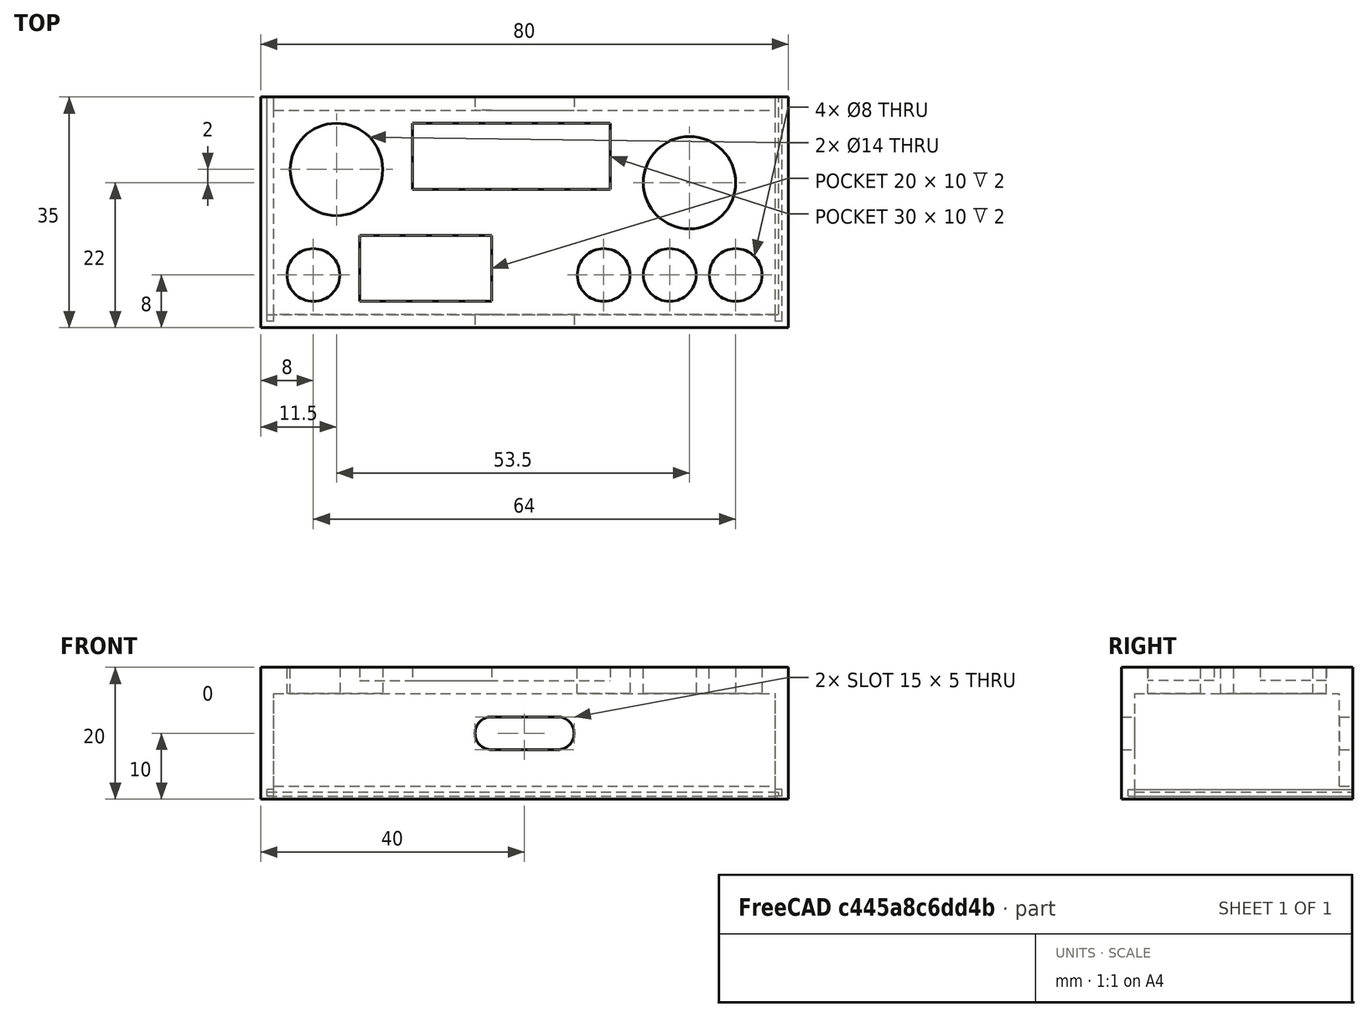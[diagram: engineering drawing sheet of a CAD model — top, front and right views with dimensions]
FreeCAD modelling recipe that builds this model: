
FCSTD DOCUMENT  (FreeCAD 1.0R39109 (Git))
Label: CriticalArtefactVersion3
License: All rights reserved
LicenseURL: https://en.wikipedia.org/wiki/All_rights_reserved
objects: Sketcher::SketchObject×5, Part::Box×5, Part::Cut×4, PartDesign::Pocket×3, Mesh::Feature×2, PartDesign::Pad×1, PartDesign::Body×1
note: 32 computed .brp shape members not serialized (recipe doc carries the construction recipe); baked Part::Feature solids carry a one-line shape summary decoded from their .brp

FEATURE [Sketcher::SketchObject] Sketch
  ArcFitTolerance = 1e-06
  AttachmentSupport = -> [XY_Plane]
  FullyConstrained = true
  MakeInternals = false
  MapMode = 5
  sketch-geometry (4):
    g0: LineSegment StartX=0 StartY=35 StartZ=0 EndX=0 EndY=0 EndZ=0
    g1: LineSegment StartX=0 StartY=0 StartZ=0 EndX=80 EndY=0 EndZ=0
    g2: LineSegment StartX=80 StartY=0 StartZ=0 EndX=80 EndY=35 EndZ=0
    g3: LineSegment StartX=80 StartY=35 StartZ=0 EndX=0 EndY=35 EndZ=0
  constraints (11):
    c: Coincident(g0,g1)
    c: Coincident(g1,g2)
    c: Coincident(g2,g3)
    c: Coincident(g3,g0)
    c: Vertical(g0)
    c: Vertical(g2)
    c: Horizontal(g1)
    c: Horizontal(g3)
    c: DistanceY(g0,g0) = 35
    c: DistanceX(g3,g3) = 80
    c: Coincident(g0,g-1)
FEATURE [PartDesign::Pad] Pad
  Direction = (0,0,1)
  Length = 20
  Length2 = 10
  Profile = -> Sketch
  ReferenceAxis = -> Sketch [N_Axis]
  Refine = true
  Suppressed = false
  Type = 0
FEATURE [Sketcher::SketchObject] Sketch001
  ArcFitTolerance = 1e-06
  AttachmentSupport = -> [Pad]
  ExternalGeometry = -> [Pad]
  FullyConstrained = true
  MakeInternals = false
  MapMode = 5
  Placement = pos=(0,0,20) rot=(0,0,1;0rad)
  sketch-geometry (6):
    g0: Circle CenterX=11.5 CenterY=24 CenterZ=0 NormalX=0 NormalY=0 NormalZ=1 AngleXU=0 Radius=7
    g1: Circle CenterX=8 CenterY=8 CenterZ=0 NormalX=0 NormalY=0 NormalZ=1 AngleXU=0 Radius=4
    g2: Circle CenterX=65 CenterY=22 CenterZ=0 NormalX=0 NormalY=0 NormalZ=1 AngleXU=0 Radius=7
    g3: Circle CenterX=52 CenterY=8 CenterZ=0 NormalX=0 NormalY=0 NormalZ=1 AngleXU=0 Radius=4
    g4: Circle CenterX=62 CenterY=8 CenterZ=0 NormalX=0 NormalY=0 NormalZ=1 AngleXU=0 Radius=4
    g5: Circle CenterX=72 CenterY=8 CenterZ=0 NormalX=0 NormalY=0 NormalZ=1 AngleXU=0 Radius=4
  constraints (18):
    c: Diameter(g0) = 14
    c: Distance(g0,g-4) = 11.5
    c: Distance(g0,g-3) = 11
    c: Diameter(g1) = 8
    c: Distance(g1,g-4) = 8
    c: Distance(g1,g-5) = 8
    c: Diameter(g2) = 14
    c: Distance(g2,g-6) = 15
    c: Distance(g2,g-3) = 13
    c: Diameter(g5) = 8
    c: Diameter(g4) = 8
    c: Diameter(g3) = 8
    c: Distance(g5,g-5) = 8
    c: Distance(g4,g-5) = 8
    c: Distance(g3,g-5) = 8
    c: Distance(g5,g-6) = 8
    c: Distance(g5,g4) = 10
    c: Distance(g3,g4) = 10
FEATURE [PartDesign::Pocket] Pocket
  BaseFeature = -> Pad
  Direction = (0,0,-1)
  Length = 33
  Length2 = 5
  Profile = -> Sketch001
  ReferenceAxis = -> Sketch001 [N_Axis]
  Refine = true
  Suppressed = false
  Type = 0
FEATURE [Sketcher::SketchObject] Sketch002
  ArcFitTolerance = 1e-06
  AttachmentSupport = -> [Pocket]
  ExternalGeometry = -> [Pocket,Sketch001]
  FullyConstrained = true
  MakeInternals = false
  MapMode = 5
  Placement = pos=(0,0,20) rot=(0,0,1;0rad)
  sketch-geometry (8):
    g0: LineSegment StartX=23 StartY=31 StartZ=0 EndX=23 EndY=21 EndZ=0
    g1: LineSegment StartX=23 StartY=21 StartZ=0 EndX=53 EndY=21 EndZ=0
    g2: LineSegment StartX=53 StartY=21 StartZ=0 EndX=53 EndY=31 EndZ=0
    g3: LineSegment StartX=53 StartY=31 StartZ=0 EndX=23 EndY=31 EndZ=0
    g4: LineSegment StartX=15 StartY=14 StartZ=0 EndX=15 EndY=4 EndZ=0
    g5: LineSegment StartX=15 StartY=4 StartZ=0 EndX=35 EndY=4 EndZ=0
    g6: LineSegment StartX=35 StartY=4 StartZ=0 EndX=35 EndY=14 EndZ=0
    g7: LineSegment StartX=35 StartY=14 StartZ=0 EndX=15 EndY=14 EndZ=0
  constraints (24):
    c: Coincident(g0,g1)
    c: Coincident(g1,g2)
    c: Coincident(g2,g3)
    c: Coincident(g3,g0)
    c: Vertical(g0)
    c: Vertical(g2)
    c: Horizontal(g1)
    c: Horizontal(g3)
    c: Coincident(g4,g5)
    c: Coincident(g5,g6)
    c: Coincident(g6,g7)
    c: Coincident(g7,g4)
    c: Vertical(g4)
    c: Vertical(g6)
    c: Horizontal(g5)
    c: Horizontal(g7)
    c: DistanceX(g3,g3) = 30
    c: DistanceX(g7,g7) = 20
    c: DistanceY(g0,g0) = 10
    c: DistanceY(g4,g4) = 10
    c: Distance(g5,g-5) = 4
    c: Distance(g2,g-3) = 4
    c: Distance(g-7,g4) = 7
    c: Distance(g0,g-4) = 23
FEATURE [PartDesign::Pocket] Pocket001
  BaseFeature = -> Pocket
  Direction = (0,0,-1)
  Length = 2
  Length2 = 5
  Profile = -> Sketch002
  ReferenceAxis = -> Sketch002 [N_Axis]
  Refine = true
  Suppressed = false
  Type = 0
FEATURE [Sketcher::SketchObject] Sketch003
  ArcFitTolerance = 1e-06
  AttachmentSupport = -> [Pocket001]
  ExternalGeometry = -> [Pocket001]
  FullyConstrained = true
  MakeInternals = false
  MapMode = 5
  Placement = pos=(0,0,0) rot=(1,0,0;1.5708rad)
  sketch-geometry (4):
    g0: ArcOfCircle CenterX=35 CenterY=10 CenterZ=0 NormalX=0 NormalY=0 NormalZ=1 AngleXU=0 Radius=2.5 StartAngle=1.5708 EndAngle=4.71239
    g1: ArcOfCircle CenterX=45 CenterY=10 CenterZ=0 NormalX=0 NormalY=0 NormalZ=1 AngleXU=0 Radius=2.5 StartAngle=4.71239 EndAngle=7.85398
    g2: LineSegment StartX=35 StartY=12.5 StartZ=0 EndX=45 EndY=12.5 EndZ=0
    g3: LineSegment StartX=35 StartY=7.5 StartZ=0 EndX=45 EndY=7.5 EndZ=0
  constraints (10):
    c: Tangent(g0,g2) = 1.5708
    c: Tangent(g0,g3) = -1.5708
    c: Tangent(g1,g2) = 1.5708
    c: Tangent(g1,g3) = -1.5708
    c: Equal(g0,g1)
    c: Horizontal(g3)
    c: Distance(g2) = 10
    c: Radius(g0) = 2.5
    c: Distance(g0,g-4) = 35
    c: Distance(g1,g-5) = 10
FEATURE [Part::Box] Box  label="Cube"
  AttacherType = Attacher::AttachEngine3D
  Height = 30
  Length = 76
  Placement = pos=(2,2,-14) rot=(0,0,1;0rad)
  Width = 31
FEATURE [Part::Box] Box001  label="Cube001"
  AttacherType = Attacher::AttachEngine3D
  Height = 2
  Length = 76
  Placement = pos=(2,33,0) rot=(0,0,1;0rad)
  Width = 2
FEATURE [PartDesign::Pocket] Pocket002
  BaseFeature = -> Pocket001
  Direction = (0,1,-2e-16)
  Length = 40
  Length2 = 5
  Profile = -> Sketch003
  ReferenceAxis = -> Sketch003 [N_Axis]
  Refine = true
  Suppressed = false
  Type = 0
FEATURE [Sketcher::SketchObject] Sketch004
  ArcFitTolerance = 1e-06
  AttachmentSupport = -> [Pocket002]
  ExternalGeometry = -> [Pocket002]
  FullyConstrained = true
  MakeInternals = false
  MapMode = 5
  Placement = pos=(0,35,0) rot=(0,0.707107,0.707107;3.14159rad)
  sketch-geometry (6):
    g0: LineSegment StartX=-1 StartY=1.5 StartZ=0 EndX=-2 EndY=1.5 EndZ=0
    g1: LineSegment StartX=-2 StartY=0.5 StartZ=0 EndX=-1 EndY=0.5 EndZ=0
    g2: LineSegment StartX=-1 StartY=0.5 StartZ=0 EndX=-1 EndY=1.5 EndZ=0
    g3: LineSegment StartX=-79 StartY=1.5 StartZ=0 EndX=-79 EndY=0.5 EndZ=0
    g4: LineSegment StartX=-79 StartY=0.5 StartZ=0 EndX=-78 EndY=0.5 EndZ=0
    g5: LineSegment StartX=-78 StartY=1.5 StartZ=0 EndX=-79 EndY=1.5 EndZ=0
  constraints (20):
    c: Coincident(g1,g2)
    c: Coincident(g2,g0)
    c: Horizontal(g0)
    c: Horizontal(g1)
    c: Vertical(g2)
    c: Distance(g1,g-6) = 0.5
    c: Coincident(g3,g4)
    c: Coincident(g5,g3)
    c: Vertical(g3)
    c: Horizontal(g4)
    c: Horizontal(g5)
    c: Distance(g3,g-6) = 0.5
    c: Distance(g3,g-3) = 1
    c: DistanceY(g3,g3) = 1
    c: Distance(g5) = 1
    c: Distance(g0) = 1
    c: Distance(g2) = 1
    c: Distance(g0,g-5) = 1
    c: Distance(g1) = 1
    c: Distance(g4) = 1
FEATURE [PartDesign::Body] Body
  AllowCompound = false
  Group = -> [Sketch,Pad,Sketch001,Pocket,Sketch002,Pocket001,Sketch003,Pocket002,Sketch004]
  Origin = -> Origin
  Tip = -> Pocket002
FEATURE [Part::Cut] Cut
  Base = -> Body
  Refine = true
  Tool = -> Box
FEATURE [Part::Cut] Cut001
  Base = -> Cut
  Refine = true
  Tool = -> Box001
FEATURE [Part::Box] Box002  label="Cube002"
  AttacherType = Attacher::AttachEngine3D
  Height = 1
  Length = 34
  Placement = pos=(2,1,0.5) rot=(0,0,1;1.5708rad)
  Width = 1
FEATURE [Part::Box] Box003  label="Cube003"
  AttacherType = Attacher::AttachEngine3D
  Height = 1
  Length = 34
  Placement = pos=(79,1,0.5) rot=(0,0,1;1.5708rad)
  Width = 1
FEATURE [Part::Cut] Cut002
  Base = -> Cut001
  Refine = true
  Tool = -> Box002
FEATURE [Part::Cut] Cut003  label="Critical Artefact"
  Base = -> Cut002
  Placement = pos=(50,0,0) rot=(0,0,1;0rad)
  Refine = true
  Tool = -> Box003
FEATURE [Part::Box] Box004  label="Lid"
  AttacherType = Attacher::AttachEngine3D
  Height = 0.6
  Length = 77.5
  Placement = pos=(51,2,0.5) rot=(0,0,1;0rad)
  Width = 33
FEATURE [Mesh::Feature] Mesh  label="Critical Artefact (Meshed)"
FEATURE [Mesh::Feature] Mesh001  label="Lid (Meshed)"
